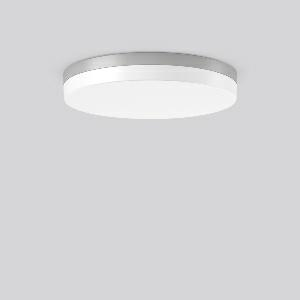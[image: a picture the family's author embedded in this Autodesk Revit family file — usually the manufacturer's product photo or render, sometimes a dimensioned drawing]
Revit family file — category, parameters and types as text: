
# Revit family: flat_slim_round_312678_004_1_19_5c64
name_source: partatom
category: Lighting Fixtures
units: mm (PartAtom-declared; Revit-internal decimal feet)

## family parameters
Cut with Voids When Loaded = No
Host = Face
Light Source = No
Part Type = Normal
Room Calculation Point = No
Round Connector Dimension = Use Diameter
Shared = No

## types (1)
- MultiLumen 1 830 (1 x LED Modul 830, 3500 lm, 3000)
    Apparent Load = 24 VA
    CIE Flux Codes = 38 68 89 85 100
    Color Rendering = 80
    Color Temperature = 3000
    Default Elevation = 1800 mm
    Height = 70 mm
    Lamp = 1 x LED Modul 830
    Lamp Light Flux = 3500 lm
    Lamp count = 1
    Length = 480 mm
    Lifetime = 50000 h
    Luminous efficacy = 146 lm/W
    Manufacturer = RZB
    ModVariant = No
    Model = 312678.004.1.19
    Mounting Place = Ceiling
    Mounting Type = Surface mounted
    Number of Poles = 1
    OnlyDefault = Yes
    Power Factor = 1
    Product Name = FLAT SLIM round
    Product group = Surface mounted ceiling and wall luminaires
    ProductGroupID = 305
    Protection Class = Protection class I
    Protection Degree = Degree of protection
    RLX_Detail_Level = 1
    RLX_Emergency_Light_Flux = 0 lm
    RLX_Emergency_Type = 0
    RLX_Emergency_Type_DB = No
    RlxData = <blob elided: 22469 chars, md5=9c7c730b>
    Socket = socket
    Standby Power = 0 W
    System Light Flux = 3500 lm
    System Power = 24 W
    Type Comments = MultiLumen 1 830
    Type Image = 312633.004.jpg
    URL = http://relux.com
    VarID = multilumen_1_830
    Voltage = 0 V
    Weight = 0.00 kg
    Width = 0 mm  [stored 0 ft]

note: [stored X ft] marks values corroborated as IEEE doubles in the binary element streams (Revit-internal decimal feet)

## geometry (parser evidence)
native form markers: Blend x4, Sweep x12
no freeform markers — native parametric forms only
